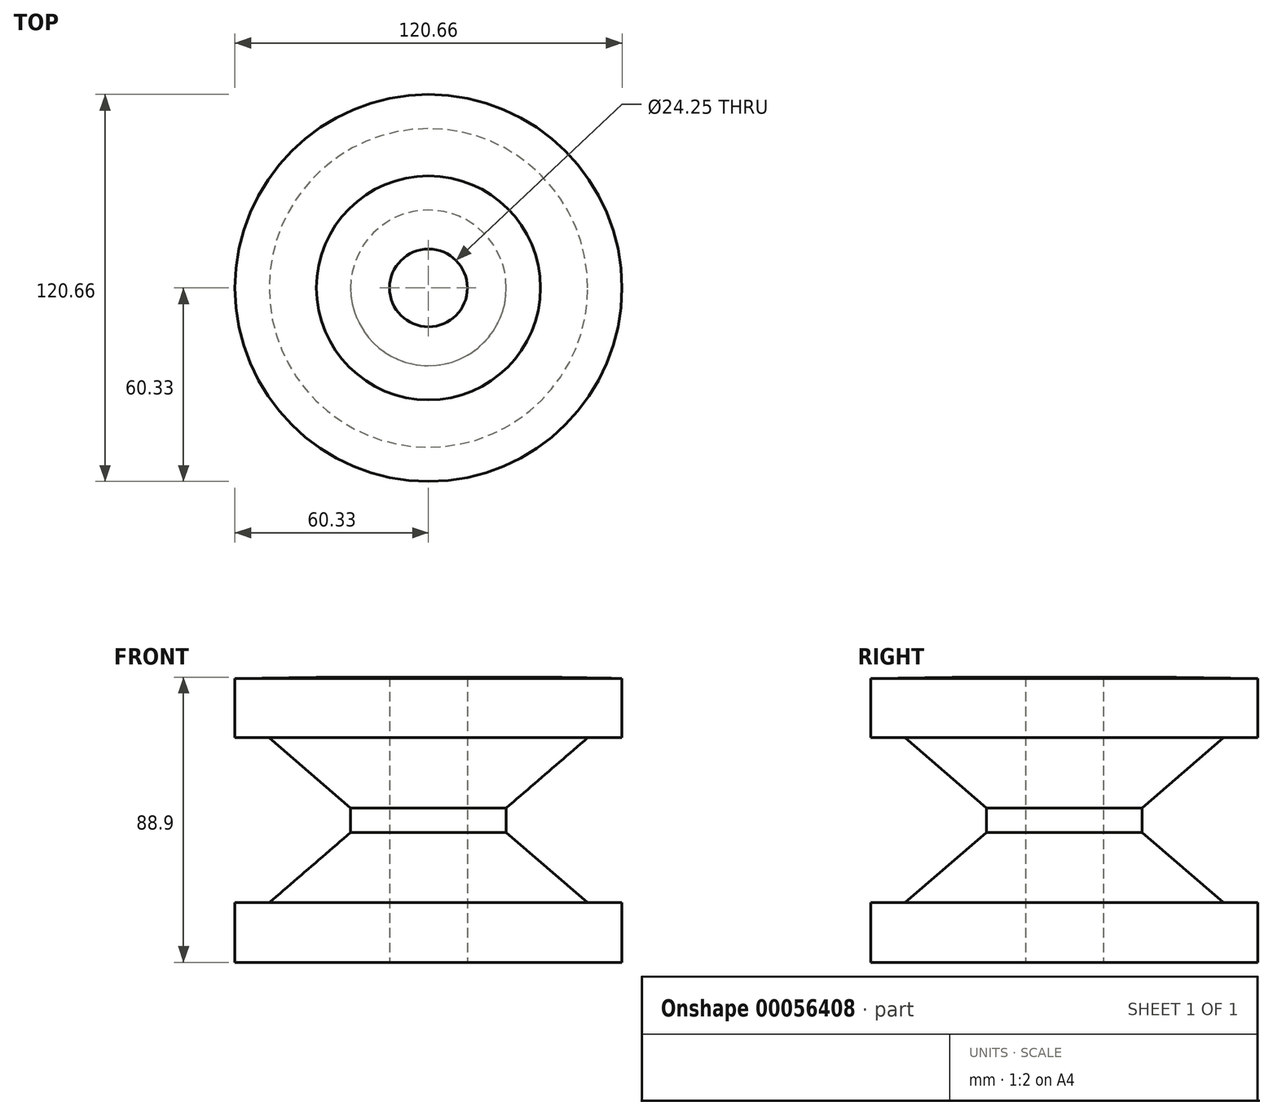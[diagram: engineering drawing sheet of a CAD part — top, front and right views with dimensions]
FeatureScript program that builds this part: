
annotation { "Feature Type Name" : "Feature", "Feature Type Description" : "" }
export const myFeature = defineFeature(function(context is Context, id is Id, definition is map)
    precondition{}
    {
        {
            var Q0;
            Q0=qCreatedBy(makeId("Front.planeOp"),FACE);
            var sketch = newSketch(context, id + "F0", { "sketchPlane" : qUnion([Q0])});
            skLineSegment(sketch, "E0.bottom", {"start": v(-60.33, 88.9) * mm, "end": v(-12.12, 88.9) * mm});
            skLineSegment(sketch, "E0.top", {"start": v(-60.33, 70.04) * mm, "end": v(-12.12, 70.04) * mm});
            skLineSegment(sketch, "E0.left", {"start": v(-60.33, 88.9) * mm, "end": v(-60.33, 70.04) * mm});
            skLineSegment(sketch, "E0.right", {"start": v(-12.12, 88.9) * mm, "end": v(-12.12, 70.04) * mm});
            skLineSegment(sketch, "E1.bottom", {"start": v(-12.12, 88.9) * mm, "end": v(-24.25, 88.9) * mm});
            skLineSegment(sketch, "E1.top", {"start": v(-12.12, 0) * mm, "end": v(-24.25, 0) * mm});
            skLineSegment(sketch, "E1.left", {"start": v(-12.12, 88.9) * mm, "end": v(-12.12, 0) * mm});
            skLineSegment(sketch, "E1.right", {"start": v(-24.25, 88.9) * mm, "end": v(-24.25, 0) * mm});
            skLineSegment(sketch, "E2.bottom", {"start": v(-12.12, 0) * mm, "end": v(-60.33, 0) * mm});
            skLineSegment(sketch, "E2.top", {"start": v(-12.12, 18.56) * mm, "end": v(-60.33, 18.56) * mm});
            skLineSegment(sketch, "E2.left", {"start": v(-12.12, 0) * mm, "end": v(-12.12, 18.56) * mm});
            skLineSegment(sketch, "E2.right", {"start": v(-60.33, 0) * mm, "end": v(-60.33, 18.56) * mm});
            skLineSegment(sketch, "E3", {"start": v(0, 0) * mm, "end": v(0, 106.58) * mm, "construction": true});
            skLineSegment(sketch, "E4", {"start": v(70.05, 0) * mm, "end": v(-112.57, 0) * mm, "construction": true});
            skPoint(sketch, "E4.endSnap0", {"position": v(-36.22, 0) * mm});
            skSolve(sketch);
        }
        {
            var Q0;
            Q0 = qSketchRegion(id + "F0", true);
            var Q1;
            Q1=sQuery(id+"F0.wireOp",EDGE,"E3");
            revolve(context, id + "F1", {"entities" : qUnion([Q0]), "axis" : qUnion([Q1]), "revolveType" : RevolveType.FULL});
        }
        {
            var Q0;
            Q0=makeQuery(id+"F1.opRevolve","SWEPT_EDGE",EDGE,{"disambiguationData":[OSD([sQuery(id+"F0.wireOp",EDGE,"E0.top"),sQuery(id+"F0.wireOp",EDGE,"E1.right")])]});
            chamfer(context, id + "F2", {"entities" : qUnion([Q0]), "chamferType" : ChamferType.TWO_OFFSETS, "width1" : 21.9 * mm, "oppositeDirection" : false, "width2" : 25.4 * mm, "tangentPropagation" : true});
        }
        {
            var Q0;
            Q0=makeQuery(id+"F1.opRevolve","SWEPT_EDGE",EDGE,{"disambiguationData":[OSD([sQuery(id+"F0.wireOp",EDGE,"E1.right"),sQuery(id+"F0.wireOp",EDGE,"E2.top")])]});
            chamfer(context, id + "F3", {"entities" : qUnion([Q0]), "chamferType" : ChamferType.TWO_OFFSETS, "width1" : 25.4 * mm, "oppositeDirection" : false, "width2" : 21.9 * mm, "tangentPropagation" : true});
        }
        {
            var Q0;
            Q0=makeQuery(id+"F1.opRevolve","SWEPT_EDGE",EDGE,{"disambiguationData":[OSD([sQuery(id+"F0.wireOp",EDGE,"E0.bottom"),sQuery(id+"F0.wireOp",EDGE,"E0.left")])]});
            chamfer(context, id + "F4", {"entities" : qUnion([Q0]), "chamferType" : ChamferType.TWO_OFFSETS, "width1" : 0.4 * mm, "oppositeDirection" : false, "width2" : 25.4 * mm, "tangentPropagation" : true});
        }
    });
